# Revit family: Genelec_4436
name_source: partatom
category: Generic Models
units: mm (PartAtom-declared; Revit-internal decimal feet)

## family parameters
Always vertical = No
Can host rebar = No
Cut with Voids When Loaded = No
Maintain Annotation Orientation = No
Part Type = Normal
Room Calculation Point = Yes
Round Connector Dimension = Use Diameter
Shared = No
Work Plane-Based = Yes

## types (1)
- 4436A
    Accuracy of Frequency Response = ± 2.5 dB (70 Hz - 20 kHz)
    Acoustic Axis = 35mm from center
    BIMobject category = Audio Electronics
    Color = <By Category>
    Connections = 1 x RJ45 AES67 / Dante Input; 1 x Euroblock Analog Input
    Crossover Frequency = 2.9 kHz
    Crossover Type = Bass/Treble
    Default Elevation = 2300 mm
    Depth = 294 mm
    Description = The Smart IP 4436A hanging pendant loudspeaker is specially designed for AV installations in open high-ceiling spaces
    Export Type to IFC As = IfcAudioVisualApplianceType
    Free field frequency response of system = 70 Hz – 20 kHz
    Frequency Response = 62 Hz - 39 kHz (-6 dB)
    Harmonic Distortion = 70…200 Hz <5 %; > 200 Hz ≤0.5 %
    Height = 237 mm
    IFC Classification = Electric Appliance
    IFC Name = 4436A
    Mains Voltage = PoE+/PoE
    Manufacturer = GENELEC
    Manufacturer Country = Finland
    Max. short term sine wave acoustic output  on axis in half space, averaged from 100Hz to 3 kHz = ≥ 104 dB SPL
    Maximum long term RMS acoustic output in same conditions with IEC weighted noise (limited by driver unit protection circuit) = ≥ 96 dB SPL
    Model = 4436A
    Model Description = Smart IP Pendant Installation Speaker
    Model Name = 4436A
    Mounting Type = Pendant
    Power Consumption = 5 W
    Power consumption Idle = 5W
    Power consumption Standby = 4W
    Product Family = Installation Speaker
    Product Group = 4000 Series Installation Speakers
    SPL = 104
    Self-generated Noise = ≤10 dB
    Show Suspension Cable = No
    Type IFC Predefined Type = SPEAKER
    Type Image = <None>
    URL = https://www.genelec.com
    Uniclass 2.0 Description = Sound Amplifiers
    Weight = 5.3
    Width = 294 mm

## geometry (parser evidence)
native form markers: Sweep x2
no freeform markers — native parametric forms only
